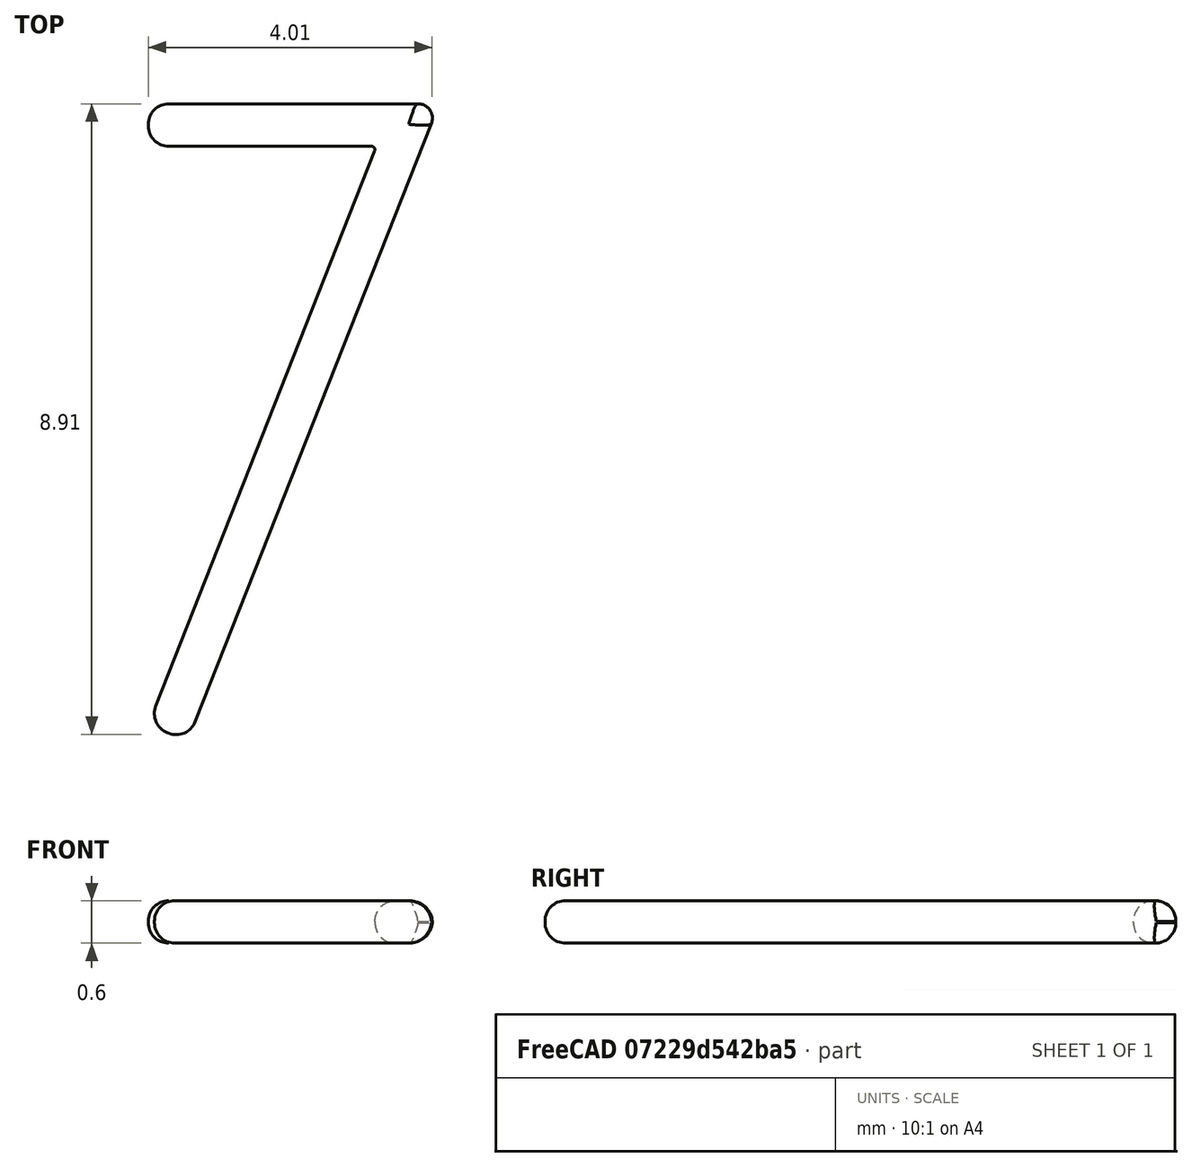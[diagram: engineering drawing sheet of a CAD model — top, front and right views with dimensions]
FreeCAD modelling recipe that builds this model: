
FCSTD DOCUMENT  (FreeCAD 0.16R6712 (Git))
Label: 7s
License: All rights reserved
LicenseURL: http://en.wikipedia.org/wiki/All_rights_reserved
objects: Sketcher::SketchObject×1, PartDesign::Pad×1, PartDesign::Fillet×1, Mesh::Feature×1
note: 4 computed .brp shape members not serialized (recipe doc carries the construction recipe); baked Part::Feature solids carry a one-line shape summary decoded from their .brp

FEATURE [Sketcher::SketchObject] Sketch
  sketch-geometry (8):
    g0: LineSegment StartX=-2 StartY=9 StartZ=0 EndX=1.81395 EndY=9 EndZ=0
    g1: LineSegment StartX=2 StartY=8.72662 StartZ=0 EndX=-1.44184 EndY=0 EndZ=0
    g2: LineSegment StartX=-2 StartY=9 StartZ=0 EndX=-2 EndY=8.4 EndZ=0
    g3: LineSegment StartX=-2 StartY=8.4 StartZ=0 EndX=1.15273 EndY=8.4 EndZ=0
    g4: LineSegment StartX=1.19924 StartY=8.33165 StartZ=0 EndX=-2 EndY=0.220141 EndZ=0
    g5: LineSegment StartX=-2 StartY=0.220141 StartZ=0 EndX=-1.44184 EndY=0 EndZ=0
    g6: ArcOfCircle CenterX=1.15273 CenterY=8.35 CenterZ=0 NormalX=0 NormalY=0 NormalZ=1 Radius=0.05 StartAngle=5.90751 EndAngle=7.85398
    g7: ArcOfCircle CenterX=1.81395 CenterY=8.8 CenterZ=0 NormalX=0 NormalY=0 NormalZ=1 Radius=0.2 StartAngle=5.90751 EndAngle=7.85398
  constraints (22):
    c: Horizontal(g0)
    c: PointOnObject(g1,g-1)
    c: Coincident(g2,g0)
    c: Coincident(g3,g2)
    c: Horizontal(g3)
    c: Coincident(g5,g1)
    c: Coincident(g4,g5)
    c: Distance(g2,g0) = 0.6
    c: Distance(g1,g4) = 0.6
    c: Perpendicular(g5,g4)
    c: Perpendicular(g3,g2)
    c: DistanceX(g-2,g0) = -2
    c: DistanceX(g-2,g4) = -2
    c: Perpendicular(g5,g1)
    c: Tangent(g3,g6) = 1.5708
    c: Tangent(g4,g6) = 1.5708
    c: Tangent(g0,g7) = 1.5708
    c: Tangent(g1,g7) = 1.5708
    c: Radius(g6) = 0.05
    c: Radius(g7) = 0.2
    c: DistanceY(g-1,g0) = 9
    c: DistanceX(g-2,g1) = 2
FEATURE [PartDesign::Pad] Pad
  Length = 0.6
  Length2 = 100
  Midplane = true
  Sketch = -> Sketch
  Type = 0
FEATURE [PartDesign::Fillet] Fillet
  Base = -> Pad [Edge4,Edge7,Edge10,Edge13,Edge16,Edge19,Edge22,Edge24,Edge3,Edge6,Edge9,Edge12,Edge15,Edge18,Edge21,Edge23,Edge1,Edge2,Edge14,Edge11]
  Radius = 0.29
FEATURE [Mesh::Feature] Mesh  label="Fillet (Meshed)"
